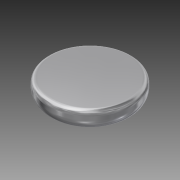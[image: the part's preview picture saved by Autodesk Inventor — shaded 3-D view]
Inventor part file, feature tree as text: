
AUTODESK INVENTOR PART (.ipt)
format: ipt  version: 2014 (Build 180170000, 170)  size: 130,048 bytes
history: native  units: in
note: dims shown in document units (in); Inventor stores cm internally (conversion verified against a paired STEP export)
features: revolve x1, sketch x1
ambient origin geometry x8: Origin, YZ Plane, XZ Plane, XY Plane, X Axis, Y Axis, Z Axis, Center Point
bodies: Solid1 (feature_tree)
feature tree (2):
  revolve  "Revolution1"  [1 undecoded]
  sketch  "Sketch1"  dims[d2=0.015in d3=0.035in d4=0.005in d5=90.0deg]
note: 1 required parameter value undecoded (feature->parameter linkage not recoverable at this tier; creation-order binding heuristic only, values carry confidence <= 0.55)
